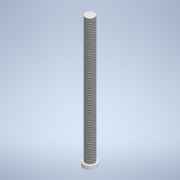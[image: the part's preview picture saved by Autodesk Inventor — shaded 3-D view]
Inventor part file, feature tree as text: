
AUTODESK INVENTOR PART (.ipt)
format: ipt  version: 2021 (Build 250183000, 183)  size: 116,736 bytes
history: native  units: mm
features: extrude x6, sketch x6, other x1, thread x1
ambient origin geometry x8: Origin, YZ Plane, XZ Plane, XY Plane, X Axis, Y Axis, Z Axis, Center Point
bodies: Body1 (feature_tree)
feature tree (14):
  other  "Sólido1"
  extrude  "Extrusión1"  Depth=2.0mm TaperAngle=0.0deg
  extrude  "Extrusión2"  Depth=5.0mm
  thread  "Rosca1"  [1 undecoded]
  extrude  "Extrusión3"  Depth=12.0mm TaperAngle=0.0deg
  extrude  "Extrusión4"  [1 undecoded]
  extrude  "Extrusión5"  [1 undecoded]
  extrude  "Extrusión6"  [1 undecoded]
  sketch  "Boceto1"  dims[d1=2.0mm d2=0.0mm d4=70.0mm d5=0.0mm]
  sketch  "Boceto2"  dims[d6=70.0mm d7=0.0mm d8=5.0mm d9=25.0mm d10=0.0mm]
  sketch  "Boceto3"  dims[d11=12.0mm d12=0.0mm d13=12.0mm d14=0.0mm]
  sketch  "Boceto4"  dims[d15=23.0mm d16=0.0mm]
  sketch  "Boceto5"
  sketch  "Boceto6"
note: 4 required parameter values undecoded (feature->parameter linkage not recoverable at this tier; creation-order binding heuristic only, values carry confidence <= 0.55)
